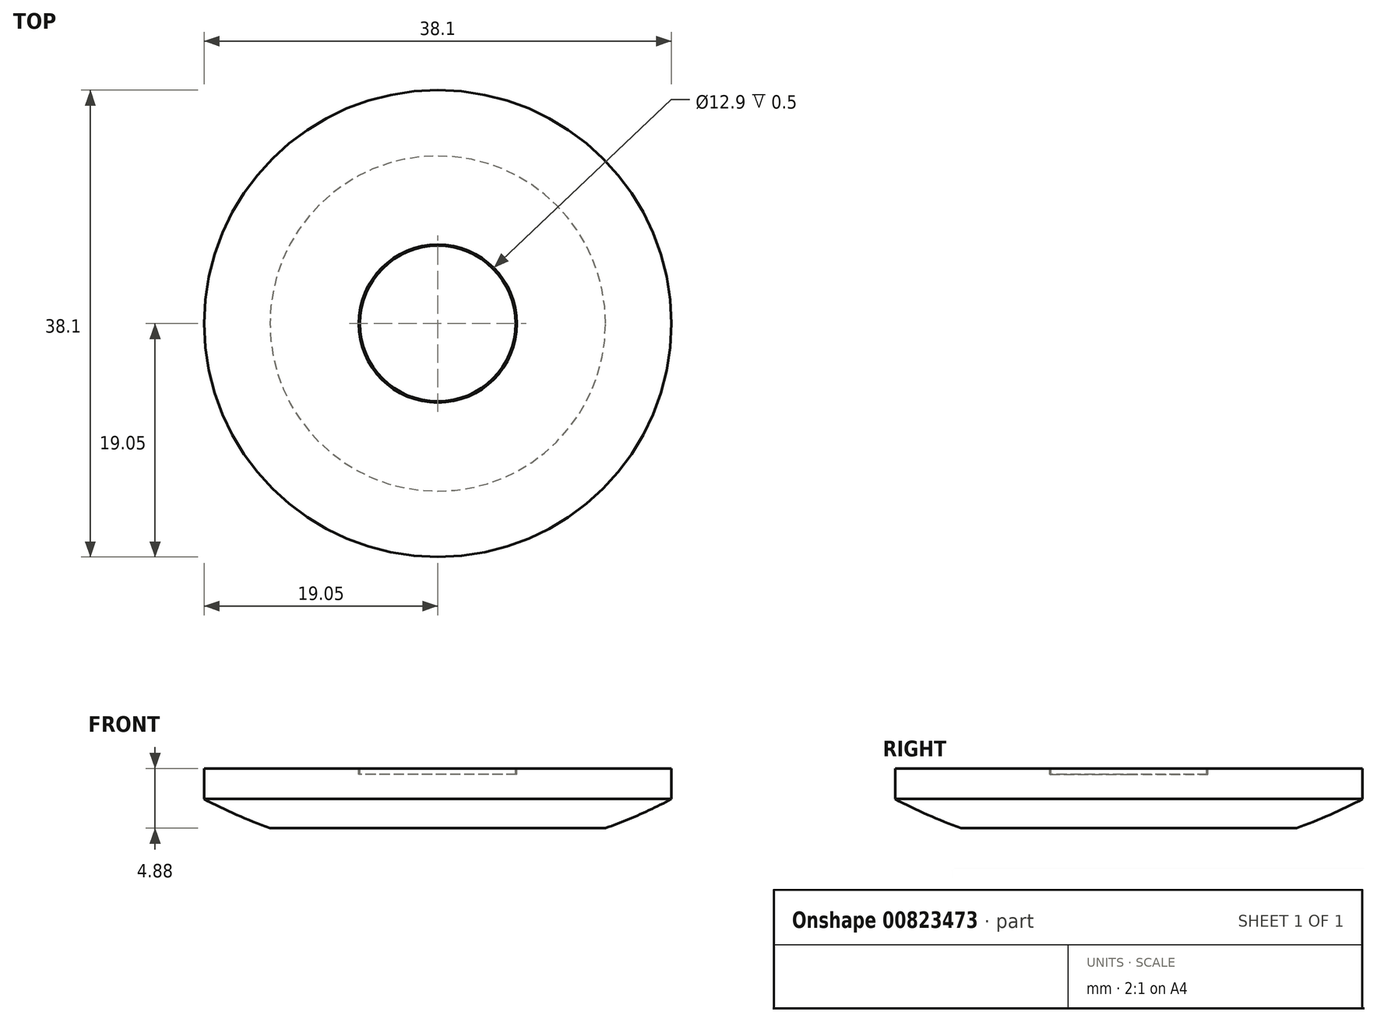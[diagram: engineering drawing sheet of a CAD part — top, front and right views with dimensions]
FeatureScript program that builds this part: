
annotation { "Feature Type Name" : "Feature", "Feature Type Description" : "" }
export const myFeature = defineFeature(function(context is Context, id is Id, definition is map)
    precondition{}
    {
        {
            var Q0;
            Q0=qCreatedBy(makeId("Top.planeOp"),FACE);
            var sketch = newSketch(context, id + "F0", { "sketchPlane" : qUnion([Q0])});
            skCircle(sketch, "E0", {"center": v(0, 0) * mm, "radius": 19.05 * mm});
            skSolve(sketch);
        }
        {
            var Q0;
            Q0=makeQuery(id+"F0.imprint","IMPRINT",FACE,{"disambiguationData":[TD([[makeQuery(id+"F0.imprint","IMPRINT",EDGE,{"derivedFrom":sQuery(id+"F0.wireOp",EDGE,"E0")}),1.0]])]});
            extrude(context, id + "F1", {"entities" : qUnion([Q0]), "depth" : 2.5 * mm, "offsetDistance" : 25 * mm});
        }
        {
            var Q0;
            Q0=makeQuery(id+"F1.opExtrude","CAP_FACE",FACE,{"disambiguationData":[OSD([sQuery(id+"F0.wireOp",EDGE,"E0")])],"isStart":false});
            var sketch = newSketch(context, id + "F2", { "sketchPlane" : qUnion([Q0])});
            skCircle(sketch, "E1", {"center": v(0, 0) * mm, "radius": 6.35 * mm});
            skCircle(sketch, "E2", {"center": v(0, 0) * mm, "radius": 6.45 * mm});
            skSolve(sketch);
        }
        {
            var Q0;
            Q0=makeQuery(id+"F2.imprint","IMPRINT",FACE,{"disambiguationData":[TD([[makeQuery(id+"F2.imprint","IMPRINT",EDGE,{"derivedFrom":sQuery(id+"F2.wireOp",EDGE,"E1")}),-1.0]])]});
            extrude(context, id + "F3", {"entities" : qUnion([Q0]), "operationType" : NewBodyOperationType.REMOVE, "oppositeDirection" : true, "depth" : .5 * mm, "offsetDistance" : 25 * mm});
        }
        {
            var Q0;
            Q0=makeQuery(id+"F2.imprint","IMPRINT",FACE,{"disambiguationData":[TD([[makeQuery(id+"F2.imprint","IMPRINT",EDGE,{"derivedFrom":sQuery(id+"F2.wireOp",EDGE,"E1")}),-1.0]])]});
            extrude(context, id + "F4", {"entities" : qUnion([Q0]), "operationType" : NewBodyOperationType.REMOVE, "oppositeDirection" : true, "depth" : .5 * mm, "offsetDistance" : 25 * mm});
        }
        {
            var Q0;
            Q0=qCreatedBy(makeId("Front.planeOp"),FACE);
            var sketch = newSketch(context, id + "F5", { "sketchPlane" : qUnion([Q0])});
            skLineSegment(sketch, "E3", {"start": v(0, 0) * mm, "end": v(0, -2.38) * mm});
            skLineSegment(sketch, "E4.0", {"start": v(-19.05, 0) * mm, "end": v(0, 0) * mm});
            skArc(sketch, "E5", {"start": v(-19.05, 0) * mm, "mid": v(-16.4, -1.28) * mm, "end": v(-13.68, -2.38) * mm});
            skLineSegment(sketch, "E6", {"start": v(0, -2.38) * mm, "end": v(-13.68, -2.38) * mm});
            skPoint(sketch, "E7.orphan", {"position": v(0, -4.75) * mm});
            skPoint(sketch, "E8.orphan", {"position": v(19.05, 0) * mm});
            skSolve(sketch);
        }
        {
            var Q0;
            Q0=makeQuery(id+"F5.imprint","IMPRINT",FACE,{"disambiguationData":[TD([[makeQuery(id+"F5.imprint","IMPRINT",EDGE,{"derivedFrom":sQuery(id+"F5.wireOp",EDGE,"E3")}),-1.0]])]});
            var Q1;
            Q1=sQuery(id+"F5.wireOp",EDGE,"E3");
            revolve(context, id + "F6", {"operationType" : NewBodyOperationType.ADD, "surfaceOperationType" : NewSurfaceOperationType.NEW, "entities" : qUnion([Q0]), "axis" : qUnion([Q1]), "revolveType" : RevolveType.FULL});
        }
    });
